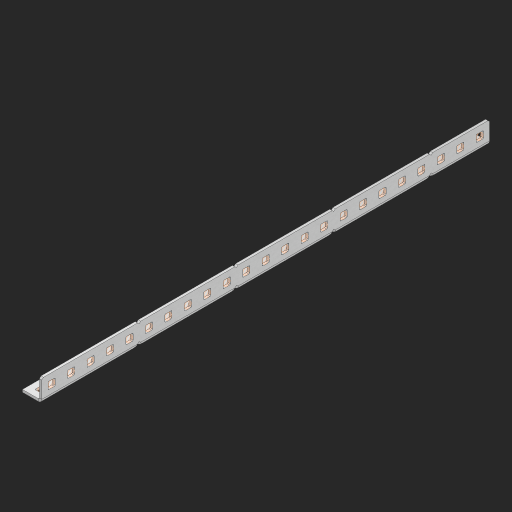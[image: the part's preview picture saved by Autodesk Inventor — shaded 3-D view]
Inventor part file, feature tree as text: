
AUTODESK INVENTOR PART (.ipt)
format: ipt  version: 2023 (Build 270158000, 158)  size: 825,856 bytes
history: native  units: in
note: dims shown in document units (in); Inventor stores cm internally (conversion verified against a paired STEP export)
features: other x51, extrude x45, sheet_metal_op x10, sketch x8, mirror x1, pattern_linear x1, chamfer x1
ambient origin geometry x8: Origin, YZ Plane, XZ Plane, XY Plane, X Axis, Y Axis, Z Axis, Center Point
bodies: Solid1 (feature_tree), Body (feature_tree)
feature tree (117):
  other  "Flange Pattern Plane"
  sheet_metal_op  "Flange Pattern"
  sheet_metal_op  "Body Pattern"
  other  "Arc Length"
  mirror  "Notch Mirror"
  pattern_linear  "Notch Pattern"  Spacing1=0.25in  [1 undecoded]
  chamfer  "End Chamfer"
  extrude  "Half Cut"  Depth=0.0625in
  sketch  "Sketch1"  dims[d0=1.5in]
  other  "Plate1"
  sketch  "Sketch2"  dims[d1=11.5in]
  other  "Plate2"
  sheet_metal_op  "Bend1"
  sheet_metal_op  "Corner1"
  sketch  "Sketch3"  dims[d2=0.0625in]
  other  "Flange Pattern Sketch"
  sketch  "Sketch7"  dims[d3=0.0625in]
  other  "Srf1"
  other  "Srf2"
  sketch  "Sketch8"  dims[d4=0.0312in]
  sketch  "Sketch9"  dims[d5=0.125in]
  other  "Srf91"
  sheet_metal_op  "Body Pattern Sketch"
  other  "Srf92"
  sketch  "Sketch13"  dims[d6=0.0625in]
  sketch  "Sketch14"  dims[d7=0.5in d8=90.0deg d9=0.0312in d10=0.25in d11=0.0625in d12=0.0625in d16=0.182in d17=0.02in d18=0.0625in d19=0.0in d20=0.25in d21=0.25in d46=0.172in d47=1.0in d48=0.0in d49=0.182in d50=0.02in d51=0.25in d52=0.25in d53=0.0625in d54=0.0in d55=0.172in d56=1.0in d57=0.0in d60=9.0551in d62=0.5in d63=0.3937in d65=0.5in d85=0.1473in d86=0.1782in d88=0.04in d89=0.0625in d90=0.0in d91=0.04in d92=0.0491in d95=2.5in d96=0.04in d97=0.25in d98=45.0deg d101=0.0in d102=2.497in d131=0.5in d132=9.0551in d134=0.5in d139=0.5in]
  other  "Srf856"
  other  "Srf1310"
  other  "Srf1311"
  other  "Srf1312"
  other  "Srf1376"
  other  "Srf1377"
  other  "Srf1728"
  other  "Srf1755"
  other  "Srf1878"
  other  "Srf1879"
  other  "Srf1880"
  other  "Srf1881"
  other  "Srf1882"
  other  "Srf1883"
  other  "Srf1884"
  other  "Srf1885"
  other  "Srf1886"
  other  "Srf1887"
  other  "Srf1888"
  other  "Srf1889"
  other  "Srf1890"
  other  "Srf1891"
  other  "Srf1892"
  other  "Srf1893"
  other  "Srf1894"
  other  "Srf1942"
  other  "Srf1943"
  other  "Srf1944"
  other  "Srf1945"
  other  "Srf1946"
  other  "Srf1947"
  other  "Srf1948"
  other  "Srf1949"
  other  "Srf1950"
  other  "Srf1951"
  other  "Srf1952"
  other  "Srf1953"
  other  "Srf1954"
  other  "Srf1955"
  other  "Srf1956"
  other  "Srf1957"
  other  "Srf1958"
  sheet_metal_op  "Flange Stamp"
  sheet_metal_op  "Flange Circle"
  sheet_metal_op  "Body Stamp"
  sheet_metal_op  "Body Circle"
  sheet_metal_op  "Notch"
  extrude  "ExtrusionSrf2"  Depth=0.0625in
  extrude  "ExtrusionSrf92"  Depth=0.5in
  extrude  "ExtrusionSrf856"  Depth=0.02in
  extrude  "ExtrusionSrf1310"  Depth=0.0625in
  extrude  "ExtrusionSrf1311"  TaperAngle=0.0deg  [1 undecoded]
  extrude  "ExtrusionSrf1312"  Depth=0.5in
  extrude  "ExtrusionSrf1376"  Depth=0.5in
  extrude  "ExtrusionSrf1377"  Depth=0.5in
  extrude  "ExtrusionSrf1728"  Depth=0.5in TaperAngle=0.0deg
  extrude  "ExtrusionSrf1755"  Depth=0.5in
  extrude  "ExtrusionSrf1878"  Depth=0.02in
  extrude  "ExtrusionSrf1879"  Depth=0.5in
  extrude  "ExtrusionSrf1880"  Depth=0.5in
  extrude  "ExtrusionSrf1881"  Depth=0.0625in
  extrude  "ExtrusionSrf1882"  TaperAngle=0.0deg  [1 undecoded]
  extrude  "ExtrusionSrf1883"  Depth=0.5in
  extrude  "ExtrusionSrf1884"  Depth=0.5in TaperAngle=0.0deg
  extrude  "ExtrusionSrf1885"  Depth=0.5in
  extrude  "ExtrusionSrf1886"  Depth=0.5in
  extrude  "ExtrusionSrf1887"  Depth=0.5in
  extrude  "ExtrusionSrf1888"  Depth=0.5in
  extrude  "ExtrusionSrf1889"  Depth=0.5in
  extrude  "ExtrusionSrf1890"  Depth=0.0625in
  extrude  "ExtrusionSrf1891"  TaperAngle=0.0deg  [1 undecoded]
  extrude  "ExtrusionSrf1892"  Depth=0.5in
  extrude  "ExtrusionSrf1893"  Depth=0.5in
  extrude  "ExtrusionSrf1894"  Depth=0.5in
  extrude  "ExtrusionSrf1942"  Depth=0.5in TaperAngle=45.0deg
  extrude  "ExtrusionSrf1943"  TaperAngle=0.0deg  [1 undecoded]
  extrude  "ExtrusionSrf1944"  Depth=0.5in
  extrude  "ExtrusionSrf1945"  Depth=0.5in
  extrude  "ExtrusionSrf1946"  Depth=0.5in
  extrude  "ExtrusionSrf1947"  Depth=0.5in
  extrude  "ExtrusionSrf1948"  Depth=0.5in
  extrude  "ExtrusionSrf1949"  [1 undecoded]
  extrude  "ExtrusionSrf1950"  [1 undecoded]
  extrude  "ExtrusionSrf1951"  [1 undecoded]
  extrude  "ExtrusionSrf1952"  [1 undecoded]
  extrude  "ExtrusionSrf1953"  [1 undecoded]
  extrude  "ExtrusionSrf1954"  [1 undecoded]
  extrude  "ExtrusionSrf1955"  [1 undecoded]
  extrude  "ExtrusionSrf1956"  [1 undecoded]
  extrude  "ExtrusionSrf1957"  [1 undecoded]
  extrude  "ExtrusionSrf1958"  [1 undecoded]
note: 15 required parameter values undecoded (feature->parameter linkage not recoverable at this tier; creation-order binding heuristic only, values carry confidence <= 0.55)
